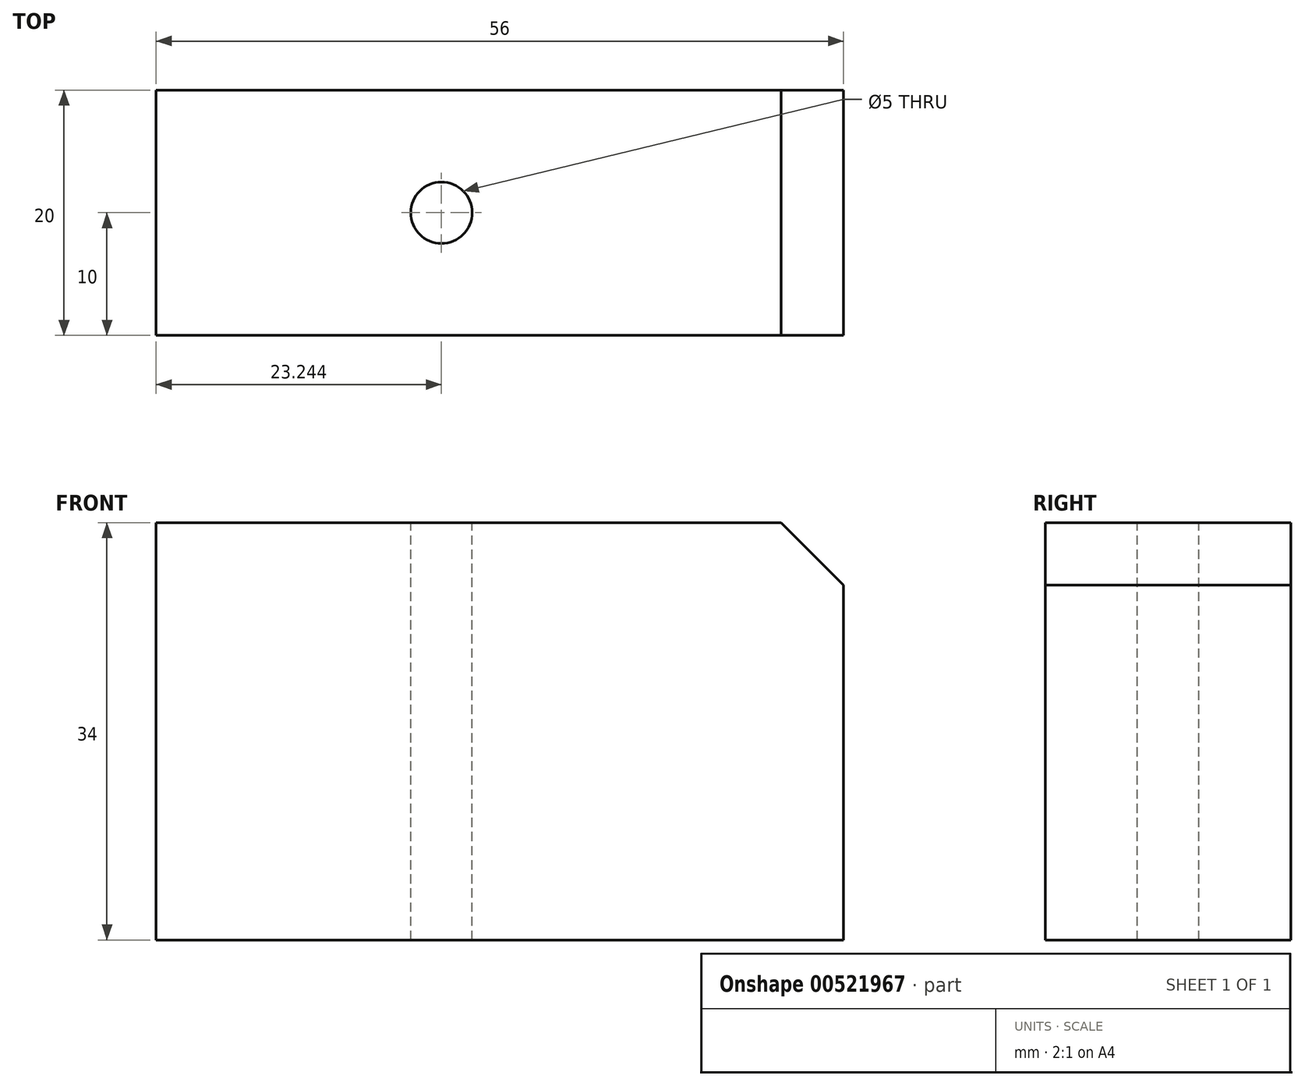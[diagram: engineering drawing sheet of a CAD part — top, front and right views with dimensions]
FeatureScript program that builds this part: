
annotation { "Feature Type Name" : "Feature", "Feature Type Description" : "" }
export const myFeature = defineFeature(function(context is Context, id is Id, definition is map)
    precondition{}
    {
        {
            var Q0;
            Q0=qCreatedBy(makeId("Front.planeOp"),FACE);
            var sketch = newSketch(context, id + "F0", { "sketchPlane" : qUnion([Q0])});
            skLineSegment(sketch, "E0.bottom", {"start": v(0, 0) * mm, "end": v(56, 0) * mm});
            skLineSegment(sketch, "E0.top", {"start": v(0, 34) * mm, "end": v(56, 34) * mm});
            skLineSegment(sketch, "E0.left", {"start": v(0, 0) * mm, "end": v(0, 34) * mm});
            skLineSegment(sketch, "E0.right", {"start": v(56, 0) * mm, "end": v(56, 34) * mm});
            skSolve(sketch);
        }
        {
            var Q0;
            Q0=makeQuery(id+"F0.imprint","IMPRINT",FACE,{"disambiguationData":[TD([[makeQuery(id+"F0.imprint","IMPRINT",EDGE,{"derivedFrom":sQuery(id+"F0.wireOp",EDGE,"E0.bottom")}),1.0]])]});
            extrude(context, id + "F1", {"entities" : qUnion([Q0]), "depth" : 20 * mm});
        }
        {
            var Q0;
            Q0=makeQuery(id+"F1.opExtrude","SWEPT_FACE",FACE,{"disambiguationData":[OSD([sQuery(id+"F0.wireOp",EDGE,"E0.top")])]});
            var sketch = newSketch(context, id + "F2", { "sketchPlane" : qUnion([Q0])});
            skCircle(sketch, "E1", {"center": v(23.24, -10) * mm, "radius": 2.5 * mm});
            skSolve(sketch);
        }
        {
            var Q0;
            Q0=sQuery(id+"F2.wireOp",VERTEX,"E1.center");
            var Q1;
            Q1=makeQuery(id+"F1.opExtrude","SWEPT_BODY",BODY,{"disambiguationData":[OSD([sQuery(id+"F0.wireOp",EDGE,"E0.bottom"),sQuery(id+"F0.wireOp",EDGE,"E0.top"),sQuery(id+"F0.wireOp",EDGE,"E0.left"),sQuery(id+"F0.wireOp",EDGE,"E0.right")])]});
            hole(context, id + "F3", {"style" : HoleStyle.SIMPLE, "endStyle" : HoleEndStyle.THROUGH, "holeDiameter" : 5 * mm, "locations" : qUnion([Q0]), "scope" : qUnion([Q1]), "tappedDepth" : 12 * mm, "tapClearance" : 3});
        }
        {
            var Q0;
            Q0=makeQuery(id+"F1.opExtrude","SWEPT_EDGE",EDGE,{"disambiguationData":[OSD([sQuery(id+"F0.wireOp",EDGE,"E0.top"),sQuery(id+"F0.wireOp",EDGE,"E0.right")])]});
            chamfer(context, id + "F4", {"entities" : qUnion([Q0]), "width" : 5.08 * mm, "tangentPropagation" : true});
        }
    });
